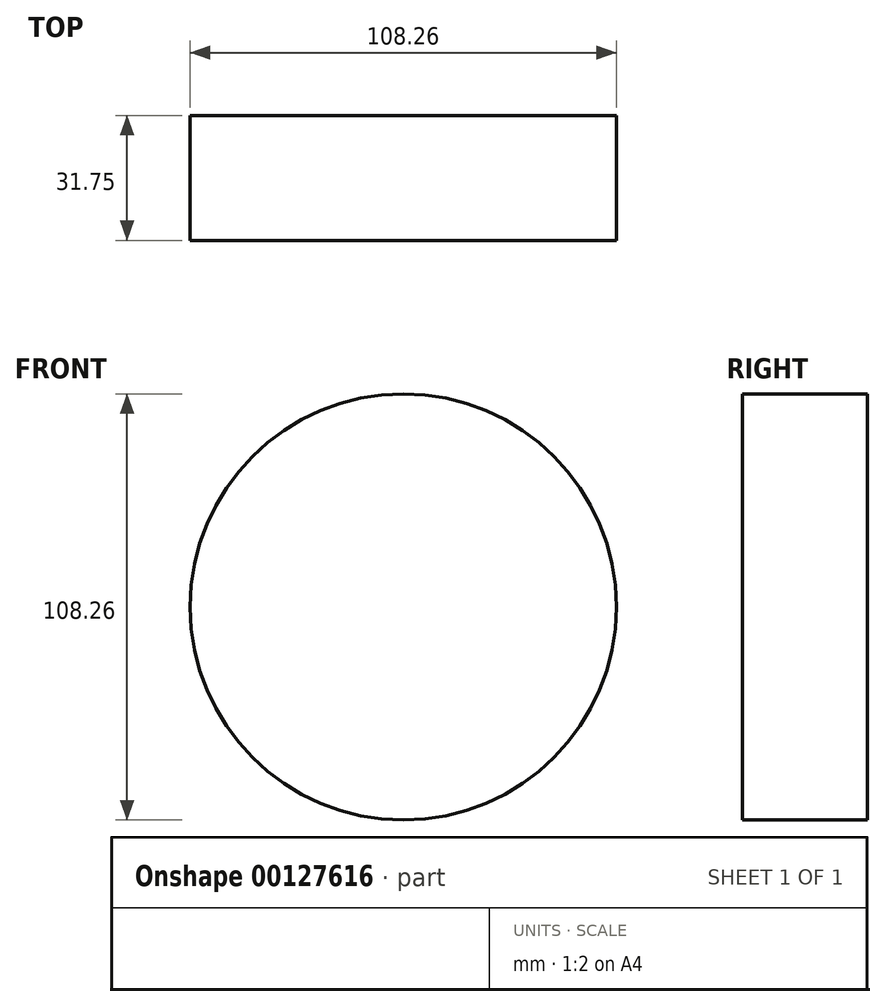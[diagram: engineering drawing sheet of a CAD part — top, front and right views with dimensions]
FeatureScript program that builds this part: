
annotation { "Feature Type Name" : "Feature", "Feature Type Description" : "" }
export const myFeature = defineFeature(function(context is Context, id is Id, definition is map)
    precondition{}
    {
        {
            var Q0;
            Q0=qCreatedBy(makeId("Front.planeOp"),FACE);
            var sketch = newSketch(context, id + "F0", { "sketchPlane" : qUnion([Q0])});
            skCircle(sketch, "E0", {"center": v(16.45, 28.96) * mm, "radius": 54.13 * mm});
            skSolve(sketch);
        }
        {
            var Q0;
            Q0=makeQuery(id+"F0.imprint","IMPRINT",FACE,{"disambiguationData":[TD([[makeQuery(id+"F0.imprint","IMPRINT",EDGE,{"derivedFrom":sQuery(id+"F0.wireOp",EDGE,"E0")}),1.0]])]});
            var Q1;
            Q1=sQuery(id+"F0.wireOp",EDGE,"E0");
            extrude(context, id + "F1", {"entities" : qUnion([Q0]), "surfaceEntities" : qUnion([Q1]), "depth" : 31.75 * mm});
        }
    });
